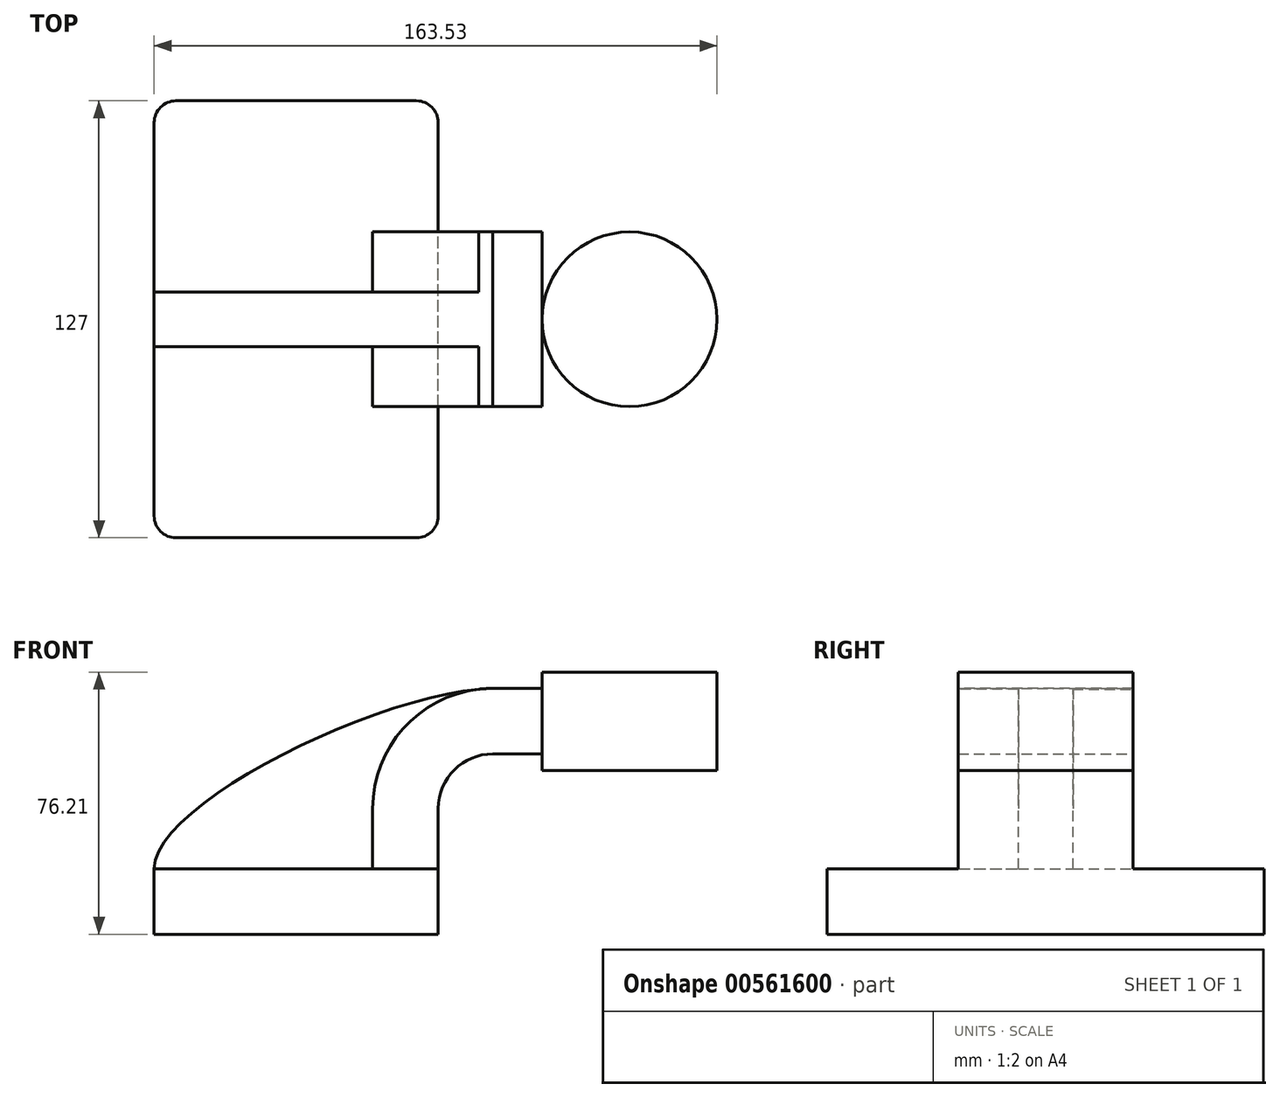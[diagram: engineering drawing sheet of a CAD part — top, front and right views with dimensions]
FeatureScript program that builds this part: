
annotation { "Feature Type Name" : "Feature", "Feature Type Description" : "" }
export const myFeature = defineFeature(function(context is Context, id is Id, definition is map)
    precondition{}
    {
        {
            var Q0;
            Q0=qCreatedBy(makeId("Front.planeOp"),FACE);
            var sketch = newSketch(context, id + "F0", { "sketchPlane" : qUnion([Q0])});
            skLineSegment(sketch, "E0.bottom", {"start": v(41.27, 9.53) * mm, "end": v(-41.28, 9.53) * mm});
            skLineSegment(sketch, "E0.top", {"start": v(41.28, -9.52) * mm, "end": v(-41.27, -9.52) * mm});
            skLineSegment(sketch, "E0.left", {"start": v(41.28, 9.53) * mm, "end": v(41.28, -9.52) * mm});
            skLineSegment(sketch, "E0.right", {"start": v(-41.28, 9.53) * mm, "end": v(-41.27, -9.52) * mm});
            skPoint(sketch, "E0.middle", {"position": v(0, 0) * mm});
            skLineSegment(sketch, "E1.bottom", {"start": v(71.45, 66.68) * mm, "end": v(122.25, 66.68) * mm});
            skLineSegment(sketch, "E1.top", {"start": v(71.45, 38.1) * mm, "end": v(122.25, 38.1) * mm});
            skLineSegment(sketch, "E1.left", {"start": v(71.45, 66.68) * mm, "end": v(71.45, 38.1) * mm});
            skLineSegment(sketch, "E1.right", {"start": v(122.25, 66.68) * mm, "end": v(122.25, 38.1) * mm});
            skPoint(sketch, "E1.middle", {"position": v(96.85, 52.39) * mm});
            skLineSegment(sketch, "E2", {"start": v(41.27, 9.53) * mm, "end": v(41.27, 27) * mm});
            skArc(sketch, "E3", {"start": v(41.27, 27) * mm, "mid": v(45.92, 38.23) * mm, "end": v(57.15, 42.88) * mm});
            skLineSegment(sketch, "E4", {"start": v(57.15, 42.88) * mm, "end": v(82.94, 42.88) * mm});
            skLineSegment(sketch, "E5.0", {"start": v(57.15, 61.93) * mm, "end": v(82.94, 61.93) * mm});
            skArc(sketch, "E5.1", {"start": v(22.23, 27) * mm, "mid": v(32.45, 51.7) * mm, "end": v(57.15, 61.93) * mm});
            skLineSegment(sketch, "E5.2", {"start": v(22.22, 9.53) * mm, "end": v(22.22, 27) * mm});
            skFitSpline(sketch, "E6", {"points": [v(-41.28, 9.52) * mm, v(57.15, 61.93) * mm], "startDerivative": vector(-0.64, 57.03) * mm, "endDerivative": vector(95.54, 1.99) * mm});
            skLineSegment(sketch, "E7", {"start": v(96.85, 38.1) * mm, "end": v(96.85, 66.68) * mm});
            skSolve(sketch);
        }
        {
            var Q0;
            Q0=makeQuery(id+"F0.imprint","IMPRINT",FACE,{"disambiguationData":[TD([[makeQuery(id+"F0.imprint","IMPRINT",EDGE,{"derivedFrom":sQuery(id+"F0.wireOp",EDGE,"E0.top")}),-1.0]])]});
            extrude(context, id + "F1", {"entities" : qUnion([Q0]), "endBound" : BoundingType.SYMMETRIC, "depth" : 127 * mm, "offsetDistance" : 25.4 * mm});
        }
        {
            var Q0;
            {var subQ1=sQuery(id+"F0.wireOp",EDGE,"E2");Q0=makeQuery(id+"F0.imprint","IMPRINT",FACE,{"disambiguationData":[TD([[makeQuery(id+"F0.imprint","IMPRINT",EDGE,{"derivedFrom":subQ1}),1.0]])]});}
            extrude(context, id + "F2", {"entities" : qUnion([Q0]), "operationType" : NewBodyOperationType.ADD, "endBound" : BoundingType.SYMMETRIC, "depth" : 50.8 * mm, "offsetDistance" : 25.4 * mm});
        }
        {
            var Q0;
            {var subQ3=sQuery(id+"F0.wireOp",EDGE,"E5.2");Q0=makeQuery(id+"F0.imprint","IMPRINT",FACE,{"disambiguationData":[TD([[makeQuery(id+"F0.imprint","IMPRINT",EDGE,{"derivedFrom":subQ3}),1.0]])]});}
            extrude(context, id + "F3", {"entities" : qUnion([Q0]), "operationType" : NewBodyOperationType.ADD, "endBound" : BoundingType.SYMMETRIC, "depth" : 15.88 * mm, "offsetDistance" : 25.4 * mm});
        }
        {
            var Q0;
            {var subQ0=sQuery(id+"F0.wireOp",EDGE,"E1.right");Q0=makeQuery(id+"F0.imprint","IMPRINT",FACE,{"disambiguationData":[TD([[makeQuery(id+"F0.imprint","IMPRINT",EDGE,{"derivedFrom":subQ0}),-1.0]])]});}
            var Q1;
            Q1=sQuery(id+"F0.wireOp",EDGE,"E7");
            revolve(context, id + "F4", {"operationType" : NewBodyOperationType.ADD, "entities" : qUnion([Q0]), "axis" : qUnion([Q1]), "revolveType" : RevolveType.FULL});
        }
        {
            var Q0;
            Q0=makeQuery(id+"F1.opExtrude","CAP_EDGE",EDGE,{"disambiguationData":[OSD([sQuery(id+"F0.wireOp",EDGE,"E0.right")])],"isStart":false});
            var Q1;
            Q1=makeQuery(id+"F1.opExtrude","CAP_EDGE",EDGE,{"disambiguationData":[OSD([sQuery(id+"F0.wireOp",EDGE,"E0.left")])],"isStart":false});
            var Q2;
            Q2=makeQuery(id+"F1.opExtrude","CAP_EDGE",EDGE,{"disambiguationData":[OSD([sQuery(id+"F0.wireOp",EDGE,"E0.left")])],"isStart":true});
            var Q3;
            Q3=makeQuery(id+"F1.opExtrude","CAP_EDGE",EDGE,{"disambiguationData":[OSD([sQuery(id+"F0.wireOp",EDGE,"E0.right")])],"isStart":true});
            fillet(context, id + "F5", {"entities" : qUnion([Q0, Q1, Q2, Q3]), "radius" : 6.35 * mm, "tangentPropagation" : true, "allowEdgeOverflow" : false});
        }
    });
